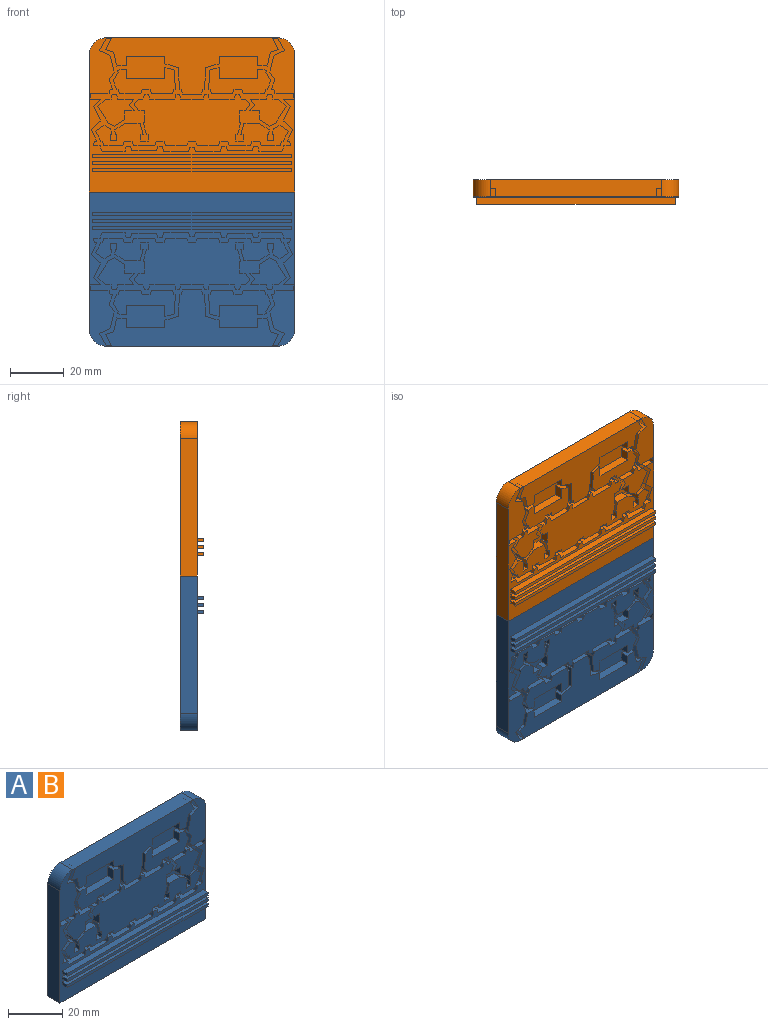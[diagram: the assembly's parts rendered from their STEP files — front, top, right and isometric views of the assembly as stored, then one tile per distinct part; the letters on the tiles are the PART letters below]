
ASSEMBLY  parts=2 mates=1
PART A: 265 faces, bbox 76.2x8.9x57.2 mm
  f0: plane 50.8x6.35mm, normal (1,0,0), area 322.6mm2, adj f2,f5,f262,f263
  f1: plane 50.8x6.35mm, normal (-1,0,0), area 322.6mm2, adj f2,f5,f262,f264
  f2: plane 76.2x57.15mm, normal (0,-1,0), area 1893.1mm2, adj f0,f1,f4,f19,f20,f21,f22,f23
  f3: plane 71.23x19.09mm, normal (0,-1,0), area 830.7mm2, adj f54,f55,f56,f57,f58,f59,f60,f61
  f4: plane 63.5x6.35mm, normal (0,0,1), area 403.2mm2, adj f2,f5,f263,f264
  f5: plane 76.2x57.15mm, normal (0,1,0), area 4337.5mm2, adj f0,f1,f4,f262,f263,f264
  f6: plane 3.18x2.01mm, normal (0.75,0,0.66), area 8.5mm2, adj f7,f125,f126,f128
  f7: plane 3.5x3.18mm, normal (0,0,-1), area 11.1mm2, adj f6,f8,f126,f128
  f8: plane 3.26x3.18mm, normal (1,0,0), area 10.4mm2, adj f7,f9,f126,f128
  f9: plane 3.89x3.18mm, normal (0.54,0,-0.84), area 14.7mm2, adj f8,f10,f126,f128
  f10: plane 3.18x2.64mm, normal (-0.42,0,-0.91), area 9.2mm2, adj f9,f11,f126,f128
  f11: plane 3.18x0.74mm, normal (-1,0,0), area 2.3mm2, adj f10,f12,f126,f128
  f12: plane 5.23x3.4mm, normal (-0.84,0,-0.54), area 19.8mm2, adj f11,f13,f126,f128
  f13: plane 3.18x2.9mm, normal (-0.73,0,0.68), area 12.6mm2, adj f12,f14,f126,f128
  f14: plane 3.18x2.21mm, normal (0,0,1), area 7mm2, adj f13,f15,f126,f128
  f15: plane 3.18x1.66mm, normal (-0.98,0,0.22), area 5.4mm2, adj f14,f16,f126,f128
  f16: plane 3.18x1.63mm, normal (0,0,1), area 5.2mm2, adj f15,f17,f126,f128
  f17: plane 3.18x1.71mm, normal (0.97,0,0.22), area 5.6mm2, adj f16,f18,f126,f128
  f18: plane 5.87x3.18mm, normal (0,0,1), area 18.6mm2, adj f17,f125,f126,f128
  f19: plane 3.34x3.18mm, normal (1,0,0), area 10.6mm2, adj f2,f20,f123,f126
  f20: plane 3.55x3.18mm, normal (0.09,0,-1), area 11.3mm2, adj f2,f19,f21,f126
  f21: plane 5.11x3.18mm, normal (-0.98,0,-0.22), area 16.6mm2, adj f2,f20,f22,f126
  f22: plane 3.18x3.02mm, normal (-0.32,0,-0.95), area 10.1mm2, adj f2,f21,f23,f126
  f23: plane 4.09x3.18mm, normal (-0.88,0,0.47), area 14.7mm2, adj f2,f22,f24,f126
  f24: plane 3.18x1.89mm, normal (0,0,-1), area 6mm2, adj f2,f23,f25,f126
  f25: plane 4.53x3.18mm, normal (0.87,0,-0.49), area 16.5mm2, adj f2,f24,f26,f126
  f26: plane 3.92x3.18mm, normal (0.38,0,0.92), area 13.5mm2, adj f2,f25,f27,f126
  f27: plane 6.3x3.18mm, normal (0.97,0,0.24), area 20.6mm2, adj f2,f26,f28,f126
  f28: plane 3.18x2.82mm, normal (0.84,0,-0.54), area 10.6mm2, adj f2,f27,f29,f126
  f29: plane 3.56x3.18mm, normal (0.95,0,0.31), area 11.9mm2, adj f2,f28,f30,f126
  f30: plane 3.18x0.85mm, normal (0,0,-1), area 2.7mm2, adj f2,f29,f31,f126
  f31: plane 3.18x1.61mm, normal (0.97,0,-0.24), area 5.3mm2, adj f2,f30,f32,f126
  f32: plane 6.85x3.18mm, normal (0,0,-1), area 21.7mm2, adj f2,f31,f33,f126
  f33: plane 3.18x2.02mm, normal (1,0,0), area 6.4mm2, adj f2,f32,f34,f126
  f34: plane 3.8x3.18mm, normal (0,0,1), area 12mm2, adj f2,f33,f35,f126
  f35: plane 3.18x2.65mm, normal (0.7,0,-0.71), area 11.8mm2, adj f2,f34,f36,f126
  f36: plane 5.53x3.18mm, normal (0.9,0,0.43), area 19.5mm2, adj f2,f35,f37,f126
  f37: plane 3.53x3.18mm, normal (0.66,0,-0.75), area 14.9mm2, adj f2,f36,f38,f126
  f38: plane 4.4x3.18mm, normal (0.92,0,0.4), area 15.3mm2, adj f2,f37,f39,f126
  f39: plane 3.18x0.74mm, normal (0,0,-1), area 2.4mm2, adj f2,f38,f40,f126
  f40: plane 3.18x1.73mm, normal (0.97,0,-0.23), area 5.6mm2, adj f2,f39,f41,f126
  f41: plane 3.18x2.55mm, normal (0,0,1), area 8.1mm2, adj f2,f40,f42,f126
  f42: plane 3.18x1.98mm, normal (0.94,0,0.34), area 6.7mm2, adj f2,f41,f43,f126
  f43: plane 8.49x3.18mm, normal (0,0,1), area 27mm2, adj f2,f42,f44,f126
  f44: plane 3.18x1.83mm, normal (-0.98,0,0.22), area 5.9mm2, adj f2,f43,f45,f126
  f45: plane 3.18x1.59mm, normal (0,0,1), area 5mm2, adj f2,f44,f46,f126
  f46: plane 3.18x1.72mm, normal (0.96,0,0.28), area 5.7mm2, adj f2,f45,f47,f126
  f47: plane 9.21x3.18mm, normal (0,0,1), area 29.3mm2, adj f2,f46,f48,f126
  f48: plane 3.18x1.77mm, normal (-0.97,0,0.25), area 5.8mm2, adj f2,f47,f49,f126
  f49: plane 3.18x1.67mm, normal (0,0,1), area 5.3mm2, adj f2,f48,f50,f126
  f50: plane 3.18x1.9mm, normal (0.96,0,0.26), area 6.3mm2, adj f2,f49,f51,f126
  f51: plane 9.18x3.18mm, normal (0,0,1), area 29.1mm2, adj f2,f50,f52,f126
  f52: plane 3.18x1.58mm, normal (-0.96,0,0.29), area 5.2mm2, adj f2,f51,f53,f126
  f53: plane 3.18x1.59mm, normal (0,0,1), area 5.1mm2, adj f2,f52,f126,f193
  f54: plane 3.18x2.87mm, normal (0,0,-1), area 9.1mm2, adj f3,f55,f126,f192
  f55: plane 3.18x1.43mm, normal (0.92,0,-0.39), area 4.9mm2, adj f3,f54,f56,f126
  f56: plane 7.75x3.18mm, normal (0,0,-1), area 24.6mm2, adj f3,f55,f57,f126
  f57: plane 3.18x1.57mm, normal (-0.94,0,-0.35), area 5.3mm2, adj f3,f56,f58,f126
  f58: plane 3.18x2.88mm, normal (0,0,-1), area 9.1mm2, adj f3,f57,f59,f126
  f59: plane 3.18x1.66mm, normal (0.95,0,-0.32), area 5.6mm2, adj f3,f58,f60,f126
  f60: plane 7.75x3.18mm, normal (0,0,-1), area 24.6mm2, adj f3,f59,f61,f126
  f61: plane 3.18x1.63mm, normal (-0.93,0,-0.37), area 5.6mm2, adj f3,f60,f62,f126
  f62: plane 3.18x2.89mm, normal (0,0,-1), area 9.2mm2, adj f3,f61,f63,f126
  f63: plane 3.18x1.59mm, normal (0.94,0,-0.35), area 5.4mm2, adj f3,f62,f64,f126
  f64: plane 7.01x3.18mm, normal (0,0,-1), area 22.3mm2, adj f3,f63,f65,f126
  f65: plane 3.18x1.66mm, normal (-0.97,0,-0.26), area 5.5mm2, adj f3,f64,f66,f126
  f66: plane 3.18x0.65mm, normal (0,0,-1), area 2.1mm2, adj f3,f65,f67,f126
  f67: plane 3.61x3.18mm, normal (-0.89,0,-0.45), area 12.8mm2, adj f3,f66,f68,f126
  f68: plane 3.18x3mm, normal (-0.61,0,0.79), area 12mm2, adj f3,f67,f69,f126
  f69: plane 3.18x2.52mm, normal (0.47,0,0.88), area 9mm2, adj f3,f68,f70,f126
  f70: plane 3.18x2.03mm, normal (0.99,0,0.1), area 6.5mm2, adj f3,f69,f71,f126
  f71: plane 3.18x0.38mm, normal (0,0,-1), area 1.2mm2, adj f3,f70,f72,f126
  f72: plane 3.18x2.39mm, normal (1,0,0), area 7.6mm2, adj f3,f71,f73,f126
  f73: plane 3.18x2.43mm, normal (0,0,1), area 7.7mm2, adj f3,f72,f74,f126
  f74: plane 3.18x2.39mm, normal (-1,0,0), area 7.6mm2, adj f3,f73,f75,f126
  f75: plane 3.18x0.57mm, normal (0,0,-1), area 1.8mm2, adj f3,f74,f76,f126
  f76: plane 3.18x1.63mm, normal (-0.99,0,-0.13), area 5.2mm2, adj f3,f75,f77,f126
  f77: plane 3.94x3.18mm, normal (-0.54,0,0.84), area 14.9mm2, adj f3,f76,f78,f126
  f78: plane 5.46x3.18mm, normal (0,0,1), area 17.3mm2, adj f3,f77,f79,f126
  f79: plane 4.19x3.18mm, normal (0.97,0,0.26), area 13.8mm2, adj f3,f78,f80,f126
  f80: plane 3.18x0.82mm, normal (0,0,-1), area 2.6mm2, adj f3,f79,f81,f126
  f81: plane 3.18x2.52mm, normal (1,0,0), area 8mm2, adj f3,f80,f82,f126
  f82: plane 3.18x2.61mm, normal (0,0,1), area 8.3mm2, adj f3,f81,f83,f126
  f83: plane 3.18x2.52mm, normal (-1,0,0), area 8mm2, adj f3,f82,f84,f126
  f84: plane 3.18x0.62mm, normal (0,0,-1), area 2mm2, adj f3,f83,f85,f126
  f85: plane 4.33x3.18mm, normal (-0.97,0,-0.26), area 14.2mm2, adj f3,f84,f86,f126
  f86: plane 3.18x0.53mm, normal (0,0,1), area 1.7mm2, adj f3,f85,f87,f126
  f87: plane 4.44x3.18mm, normal (-1,0,0), area 14.1mm2, adj f3,f86,f88,f126
  f88: plane 3.18x2.2mm, normal (0,0,-1), area 7mm2, adj f3,f87,f89,f126
  f89: plane 3.18x2.35mm, normal (-0.81,0,-0.59), area 9.2mm2, adj f3,f88,f90,f126
  f90: plane 3.18x1.95mm, normal (-0.79,0,0.62), area 7.9mm2, adj f3,f89,f91,f126
  f91: plane 3.18x1.76mm, normal (0,0,1), area 5.6mm2, adj f3,f90,f92,f126
  f92: plane 3.18x1.74mm, normal (-0.95,0,0.31), area 5.8mm2, adj f3,f91,f93,f126
  f93: plane 3.18x1.41mm, normal (0,0,1), area 4.5mm2, adj f3,f92,f94,f126
  f94: plane 3.18x1.78mm, normal (0.95,0,0.3), area 5.9mm2, adj f3,f93,f95,f126
  f95: plane 9.25x3.18mm, normal (0,0,1), area 29.4mm2, adj f3,f94,f96,f126
  f96: plane 3.18x1.79mm, normal (-0.97,0,0.23), area 5.8mm2, adj f3,f95,f97,f126
  f97: plane 3.18x1.4mm, normal (0,0,1), area 4.4mm2, adj f3,f96,f98,f126
  f98: plane 3.18x1.79mm, normal (0.97,0,0.24), area 5.8mm2, adj f3,f97,f99,f126
  f99: plane 8.24x3.18mm, normal (0,0,1), area 26.2mm2, adj f3,f98,f126,f149
  f100: plane 7.08x3.18mm, normal (0,0,-1), area 22.5mm2, adj f2,f101,f126,f148
  f101: plane 3.18x1.81mm, normal (-0.97,0,-0.26), area 5.9mm2, adj f2,f100,f102,f126
  f102: plane 3.18x0.62mm, normal (0,0,-1), area 2mm2, adj f2,f101,f103,f126
  f103: plane 8.01x3.18mm, normal (-1,0,-0.05), area 25.5mm2, adj f2,f102,f104,f126
  f104: plane 4.97x3.18mm, normal (-0.28,0,-0.96), area 16.4mm2, adj f2,f103,f105,f126
  f105: plane 3.18x2.85mm, normal (-1,0,0), area 9mm2, adj f2,f104,f123,f126
  f106: plane 3.18x3.13mm, normal (-0.12,0,0.99), area 10mm2, adj f107,f124,f126,f127
  f107: plane 3.51x3.18mm, normal (1,0,0), area 11.1mm2, adj f106,f108,f126,f127
  f108: plane 14.32x3.18mm, normal (0,0,1), area 45.5mm2, adj f107,f109,f126,f127
  f109: plane 4.18x3.18mm, normal (-1,0,0), area 13.3mm2, adj f108,f110,f126,f127
  f110: plane 3.51x3.18mm, normal (0.29,0,0.96), area 11.6mm2, adj f109,f111,f126,f127
  f111: plane 7.06x3.18mm, normal (1,0,0.05), area 22.4mm2, adj f110,f112,f126,f127
  f112: plane 3.18x0.6mm, normal (0,0,-1), area 1.9mm2, adj f111,f113,f126,f127
  f113: plane 3.18x1.65mm, normal (0.97,0,-0.22), area 5.4mm2, adj f112,f114,f126,f127
  f114: plane 7.82x3.18mm, normal (0,0,-1), area 24.8mm2, adj f113,f115,f126,f127
  f115: plane 3.18x1.65mm, normal (-0.95,0,-0.32), area 5.5mm2, adj f114,f116,f126,f127
  f116: plane 3.18x2.96mm, normal (0,0,-1), area 9.4mm2, adj f115,f117,f126,f127
  f117: plane 3.18x1.69mm, normal (0.96,0,-0.29), area 5.6mm2, adj f116,f118,f126,f127
  f118: plane 7.77x3.18mm, normal (0,0,-1), area 24.7mm2, adj f117,f119,f126,f127
  f119: plane 3.18x1.69mm, normal (-0.94,0,-0.34), area 5.7mm2, adj f118,f120,f126,f127
  f120: plane 3.18x0.57mm, normal (0,0,-1), area 1.8mm2, adj f119,f121,f126,f127
  f121: plane 3.18x3.13mm, normal (-0.94,0,-0.35), area 10.6mm2, adj f120,f122,f126,f127
  f122: plane 3.18x3.08mm, normal (-0.87,0,0.49), area 11.2mm2, adj f121,f124,f126,f127
  f123: plane 14.32x3.18mm, normal (0,0,-1), area 45.5mm2, adj f2,f19,f105,f126
  f124: plane 3.18x0.85mm, normal (-0.99,0,-0.12), area 2.7mm2, adj f106,f122,f126,f127
  f125: plane 3.18x2.24mm, normal (0.82,0,-0.57), area 8.6mm2, adj f6,f18,f126,f128
  f126: plane 75.21x41.83mm, normal (0,-1,0), area 876.6mm2, adj f6,f7,f8,f9,f10,f11,f12,f13
  f127: plane 22.95x9.8mm, normal (0,-1,0), area 140.1mm2, adj f106,f107,f108,f109,f110,f111,f112,f113
  f128: plane 13.42x11.75mm, normal (0,-1,0), area 88.1mm2, adj f6,f7,f8,f9,f10,f11,f12,f13
  f129: plane 3.18x2.01mm, normal (-0.75,0,0.66), area 8.5mm2, adj f126,f130,f244,f246
  f130: plane 3.18x2.24mm, normal (-0.82,0,-0.57), area 8.6mm2, adj f126,f129,f131,f246
  f131: plane 5.87x3.18mm, normal (0,0,1), area 18.6mm2, adj f126,f130,f132,f246
  f132: plane 3.18x1.71mm, normal (-0.97,0,0.22), area 5.6mm2, adj f126,f131,f133,f246
  f133: plane 3.18x1.63mm, normal (0,0,1), area 5.2mm2, adj f126,f132,f134,f246
  f134: plane 3.18x1.66mm, normal (0.98,0,0.22), area 5.4mm2, adj f126,f133,f135,f246
  f135: plane 3.18x2.21mm, normal (0,0,1), area 7mm2, adj f126,f134,f136,f246
  f136: plane 3.18x2.9mm, normal (0.73,0,0.68), area 12.6mm2, adj f126,f135,f137,f246
  f137: plane 5.23x3.4mm, normal (0.84,0,-0.54), area 19.8mm2, adj f126,f136,f138,f246
  f138: plane 3.18x0.74mm, normal (1,0,0), area 2.3mm2, adj f126,f137,f139,f246
  f139: plane 3.18x2.64mm, normal (0.42,0,-0.91), area 9.2mm2, adj f126,f138,f140,f246
  f140: plane 3.89x3.18mm, normal (-0.54,0,-0.84), area 14.7mm2, adj f126,f139,f141,f246
  f141: plane 3.26x3.18mm, normal (-1,0,0), area 10.4mm2, adj f126,f140,f244,f246
  f142: plane 3.34x3.18mm, normal (-1,0,0), area 10.6mm2, adj f2,f126,f143,f242
  f143: plane 14.32x3.18mm, normal (0,0,-1), area 45.5mm2, adj f2,f126,f142,f144
  f144: plane 3.18x2.85mm, normal (1,0,0), area 9mm2, adj f2,f126,f143,f145
  f145: plane 4.97x3.18mm, normal (0.28,0,-0.96), area 16.4mm2, adj f2,f126,f144,f146
  f146: plane 8.01x3.18mm, normal (1,0,-0.05), area 25.5mm2, adj f2,f126,f145,f147
  f147: plane 3.18x0.62mm, normal (0,0,-1), area 2mm2, adj f2,f126,f146,f148
  f148: plane 3.18x1.81mm, normal (0.97,0,-0.26), area 5.9mm2, adj f2,f100,f126,f147
  f149: plane 3.18x1.79mm, normal (-0.97,0,0.24), area 5.8mm2, adj f3,f99,f126,f150
  f150: plane 3.18x1.4mm, normal (0,0,1), area 4.4mm2, adj f3,f126,f149,f151
  f151: plane 3.18x1.79mm, normal (0.97,0,0.23), area 5.8mm2, adj f3,f126,f150,f152
  f152: plane 9.25x3.18mm, normal (0,0,1), area 29.4mm2, adj f3,f126,f151,f153
  f153: plane 3.18x1.78mm, normal (-0.95,0,0.3), area 5.9mm2, adj f3,f126,f152,f154
  f154: plane 3.18x1.41mm, normal (0,0,1), area 4.5mm2, adj f3,f126,f153,f155
  f155: plane 3.18x1.74mm, normal (0.95,0,0.31), area 5.8mm2, adj f3,f126,f154,f156
  f156: plane 3.18x1.76mm, normal (0,0,1), area 5.6mm2, adj f3,f126,f155,f157
  f157: plane 3.18x1.95mm, normal (0.79,0,0.62), area 7.9mm2, adj f3,f126,f156,f158
  f158: plane 3.18x2.35mm, normal (0.81,0,-0.59), area 9.2mm2, adj f3,f126,f157,f159
  f159: plane 3.18x2.2mm, normal (0,0,-1), area 7mm2, adj f3,f126,f158,f160
  f160: plane 4.44x3.18mm, normal (1,0,0), area 14.1mm2, adj f3,f126,f159,f161
  f161: plane 3.18x0.53mm, normal (0,0,1), area 1.7mm2, adj f3,f126,f160,f162
  f162: plane 4.33x3.18mm, normal (0.97,0,-0.26), area 14.2mm2, adj f3,f126,f161,f163
  f163: plane 3.18x0.62mm, normal (0,0,-1), area 2mm2, adj f3,f126,f162,f164
  f164: plane 3.18x2.52mm, normal (1,0,0), area 8mm2, adj f3,f126,f163,f165
  f165: plane 3.18x2.61mm, normal (0,0,1), area 8.3mm2, adj f3,f126,f164,f166
  f166: plane 3.18x2.52mm, normal (-1,0,0), area 8mm2, adj f3,f126,f165,f167
  f167: plane 3.18x0.82mm, normal (0,0,-1), area 2.6mm2, adj f3,f126,f166,f168
  f168: plane 4.19x3.18mm, normal (-0.97,0,0.26), area 13.8mm2, adj f3,f126,f167,f169
  f169: plane 5.46x3.18mm, normal (0,0,1), area 17.3mm2, adj f3,f126,f168,f170
  f170: plane 3.94x3.18mm, normal (0.54,0,0.84), area 14.9mm2, adj f3,f126,f169,f171
  f171: plane 3.18x1.63mm, normal (0.99,0,-0.13), area 5.2mm2, adj f3,f126,f170,f172
  f172: plane 3.18x0.57mm, normal (0,0,-1), area 1.8mm2, adj f3,f126,f171,f173
  f173: plane 3.18x2.39mm, normal (1,0,0), area 7.6mm2, adj f3,f126,f172,f174
  f174: plane 3.18x2.43mm, normal (0,0,1), area 7.7mm2, adj f3,f126,f173,f175
  f175: plane 3.18x2.39mm, normal (-1,0,0), area 7.6mm2, adj f3,f126,f174,f176
  f176: plane 3.18x0.38mm, normal (0,0,-1), area 1.2mm2, adj f3,f126,f175,f177
  f177: plane 3.18x2.03mm, normal (-0.99,0,0.1), area 6.5mm2, adj f3,f126,f176,f178
  f178: plane 3.18x2.52mm, normal (-0.47,0,0.88), area 9mm2, adj f3,f126,f177,f179
  f179: plane 3.18x3mm, normal (0.61,0,0.79), area 12mm2, adj f3,f126,f178,f180
  f180: plane 3.61x3.18mm, normal (0.89,0,-0.45), area 12.8mm2, adj f3,f126,f179,f181
  f181: plane 3.18x0.65mm, normal (0,0,-1), area 2.1mm2, adj f3,f126,f180,f182
  f182: plane 3.18x1.66mm, normal (0.97,0,-0.26), area 5.5mm2, adj f3,f126,f181,f183
  f183: plane 7.01x3.18mm, normal (0,0,-1), area 22.3mm2, adj f3,f126,f182,f184
  f184: plane 3.18x1.59mm, normal (-0.94,0,-0.35), area 5.4mm2, adj f3,f126,f183,f185
  f185: plane 3.18x2.89mm, normal (0,0,-1), area 9.2mm2, adj f3,f126,f184,f186
  f186: plane 3.18x1.63mm, normal (0.93,0,-0.37), area 5.6mm2, adj f3,f126,f185,f187
  f187: plane 7.75x3.18mm, normal (0,0,-1), area 24.6mm2, adj f3,f126,f186,f188
  f188: plane 3.18x1.66mm, normal (-0.95,0,-0.32), area 5.6mm2, adj f3,f126,f187,f189
  f189: plane 3.18x2.88mm, normal (0,0,-1), area 9.1mm2, adj f3,f126,f188,f190
  f190: plane 3.18x1.57mm, normal (0.94,0,-0.35), area 5.3mm2, adj f3,f126,f189,f191
  f191: plane 7.75x3.18mm, normal (0,0,-1), area 24.6mm2, adj f3,f126,f190,f192
  f192: plane 3.18x1.43mm, normal (-0.92,0,-0.39), area 4.9mm2, adj f3,f54,f126,f191
  f193: plane 3.18x1.58mm, normal (0.96,0,0.29), area 5.2mm2, adj f2,f53,f126,f194
  f194: plane 9.18x3.18mm, normal (0,0,1), area 29.1mm2, adj f2,f126,f193,f195
  f195: plane 3.18x1.9mm, normal (-0.96,0,0.26), area 6.3mm2, adj f2,f126,f194,f196
  f196: plane 3.18x1.67mm, normal (0,0,1), area 5.3mm2, adj f2,f126,f195,f197
  f197: plane 3.18x1.77mm, normal (0.97,0,0.25), area 5.8mm2, adj f2,f126,f196,f198
  f198: plane 9.21x3.18mm, normal (0,0,1), area 29.3mm2, adj f2,f126,f197,f199
  f199: plane 3.18x1.72mm, normal (-0.96,0,0.28), area 5.7mm2, adj f2,f126,f198,f200
  f200: plane 3.18x1.59mm, normal (0,0,1), area 5mm2, adj f2,f126,f199,f201
  f201: plane 3.18x1.83mm, normal (0.98,0,0.22), area 5.9mm2, adj f2,f126,f200,f202
  f202: plane 8.49x3.18mm, normal (0,0,1), area 27mm2, adj f2,f126,f201,f203
  f203: plane 3.18x1.98mm, normal (-0.94,0,0.34), area 6.7mm2, adj f2,f126,f202,f204
  f204: plane 3.18x2.55mm, normal (0,0,1), area 8.1mm2, adj f2,f126,f203,f205
  f205: plane 3.18x1.73mm, normal (-0.97,0,-0.23), area 5.6mm2, adj f2,f126,f204,f206
  f206: plane 3.18x0.74mm, normal (0,0,-1), area 2.4mm2, adj f2,f126,f205,f207
  f207: plane 4.4x3.18mm, normal (-0.92,0,0.4), area 15.3mm2, adj f2,f126,f206,f208
  f208: plane 3.53x3.18mm, normal (-0.66,0,-0.75), area 14.9mm2, adj f2,f126,f207,f209
  f209: plane 5.53x3.18mm, normal (-0.9,0,0.43), area 19.5mm2, adj f2,f126,f208,f210
  f210: plane 3.18x2.65mm, normal (-0.7,0,-0.71), area 11.8mm2, adj f2,f126,f209,f211
  f211: plane 3.8x3.18mm, normal (0,0,1), area 12mm2, adj f2,f126,f210,f212
  f212: plane 3.18x2.02mm, normal (-1,0,0), area 6.4mm2, adj f2,f126,f211,f213
  f213: plane 6.85x3.18mm, normal (0,0,-1), area 21.7mm2, adj f2,f126,f212,f214
  f214: plane 3.18x1.61mm, normal (-0.97,0,-0.24), area 5.3mm2, adj f2,f126,f213,f215
  f215: plane 3.18x0.85mm, normal (0,0,-1), area 2.7mm2, adj f2,f126,f214,f216
  f216: plane 3.56x3.18mm, normal (-0.95,0,0.31), area 11.9mm2, adj f2,f126,f215,f217
  f217: plane 3.18x2.82mm, normal (-0.84,0,-0.54), area 10.6mm2, adj f2,f126,f216,f218
  f218: plane 6.3x3.18mm, normal (-0.97,0,0.24), area 20.6mm2, adj f2,f126,f217,f219
  f219: plane 3.92x3.18mm, normal (-0.38,0,0.92), area 13.5mm2, adj f2,f126,f218,f220
  f220: plane 4.53x3.18mm, normal (-0.87,0,-0.49), area 16.5mm2, adj f2,f126,f219,f221
  f221: plane 3.18x1.89mm, normal (0,0,-1), area 6mm2, adj f2,f126,f220,f222
  f222: plane 4.09x3.18mm, normal (0.88,0,0.47), area 14.7mm2, adj f2,f126,f221,f223
  f223: plane 3.18x3.02mm, normal (0.32,0,-0.95), area 10.1mm2, adj f2,f126,f222,f224
  f224: plane 5.11x3.18mm, normal (0.98,0,-0.22), area 16.6mm2, adj f2,f126,f223,f242
  f225: plane 3.18x3.13mm, normal (0.12,0,0.99), area 10mm2, adj f126,f226,f243,f245
  f226: plane 3.18x0.85mm, normal (0.99,0,-0.12), area 2.7mm2, adj f126,f225,f227,f245
  f227: plane 3.18x3.08mm, normal (0.87,0,0.49), area 11.2mm2, adj f126,f226,f228,f245
  f228: plane 3.18x3.13mm, normal (0.94,0,-0.35), area 10.6mm2, adj f126,f227,f229,f245
  f229: plane 3.18x0.57mm, normal (0,0,-1), area 1.8mm2, adj f126,f228,f230,f245
  f230: plane 3.18x1.69mm, normal (0.94,0,-0.34), area 5.7mm2, adj f126,f229,f231,f245
  f231: plane 7.77x3.18mm, normal (0,0,-1), area 24.7mm2, adj f126,f230,f232,f245
  f232: plane 3.18x1.69mm, normal (-0.96,0,-0.29), area 5.6mm2, adj f126,f231,f233,f245
  f233: plane 3.18x2.96mm, normal (0,0,-1), area 9.4mm2, adj f126,f232,f234,f245
  f234: plane 3.18x1.65mm, normal (0.95,0,-0.32), area 5.5mm2, adj f126,f233,f235,f245
  f235: plane 7.82x3.18mm, normal (0,0,-1), area 24.8mm2, adj f126,f234,f236,f245
  f236: plane 3.18x1.65mm, normal (-0.97,0,-0.22), area 5.4mm2, adj f126,f235,f237,f245
  f237: plane 3.18x0.6mm, normal (0,0,-1), area 1.9mm2, adj f126,f236,f238,f245
  f238: plane 7.06x3.18mm, normal (-1,0,0.05), area 22.4mm2, adj f126,f237,f239,f245
  f239: plane 3.51x3.18mm, normal (-0.29,0,0.96), area 11.6mm2, adj f126,f238,f240,f245
  f240: plane 4.18x3.18mm, normal (1,0,0), area 13.3mm2, adj f126,f239,f241,f245
  f241: plane 14.32x3.18mm, normal (0,0,1), area 45.5mm2, adj f126,f240,f243,f245
  f242: plane 3.55x3.18mm, normal (-0.09,0,-1), area 11.3mm2, adj f2,f126,f142,f224
  f243: plane 3.51x3.18mm, normal (-1,0,0), area 11.1mm2, adj f126,f225,f241,f245
  f244: plane 3.5x3.18mm, normal (0,0,-1), area 11.1mm2, adj f126,f129,f141,f246
  f245: plane 22.95x9.8mm, normal (0,-1,0), area 140.1mm2, adj f225,f226,f227,f228,f229,f230,f231,f232
  f246: plane 13.42x11.75mm, normal (0,-1,0), area 88.1mm2, adj f129,f130,f131,f132,f133,f134,f135,f136
  f247: plane 2.54x1.27mm, normal (-1,0,0), area 3.2mm2, adj f2,f248,f250,f251
  f248: plane 73.66x2.54mm, normal (0,0,-1), area 187.1mm2, adj f2,f247,f249,f251
  f249: plane 2.54x1.27mm, normal (1,0,0), area 3.2mm2, adj f2,f248,f250,f251
  f250: plane 73.66x2.54mm, normal (0,0,1), area 187.1mm2, adj f2,f247,f249,f251
  f251: plane 73.66x1.27mm, normal (0,-1,0), area 93.5mm2, adj f247,f248,f249,f250
  f252: plane 73.66x2.54mm, normal (0,0,-1), area 187.1mm2, adj f2,f253,f255,f256
  f253: plane 2.54x1.27mm, normal (1,0,0), area 3.2mm2, adj f2,f252,f254,f256
  f254: plane 73.66x2.54mm, normal (0,0,1), area 187.1mm2, adj f2,f253,f255,f256
  f255: plane 2.54x1.27mm, normal (-1,0,0), area 3.2mm2, adj f2,f252,f254,f256
  f256: plane 73.66x1.27mm, normal (0,-1,0), area 93.5mm2, adj f252,f253,f254,f255
  f257: plane 2.54x1.27mm, normal (1,0,0), area 3.2mm2, adj f2,f258,f260,f261
  f258: plane 73.66x2.54mm, normal (0,0,1), area 187.1mm2, adj f2,f257,f259,f261
  f259: plane 2.54x1.27mm, normal (-1,0,0), area 3.2mm2, adj f2,f258,f260,f261
  f260: plane 73.66x2.54mm, normal (0,0,-1), area 187.1mm2, adj f2,f257,f259,f261
  f261: plane 73.66x1.27mm, normal (0,-1,0), area 93.5mm2, adj f257,f258,f259,f260
  f262: plane 76.2x6.35mm, normal (0,0,-1), area 483.9mm2, adj f0,f1,f2,f5
  f263: cylinder r=6.35mm len=6.35mm, axis (0,1,0), area 63.3mm2, adj f0,f2,f4,f5
  f264: cylinder r=6.35mm len=6.35mm, axis (0,-1,0), area 63.3mm2, adj f1,f2,f4,f5
PART B: same geometry as A
PLACE A rot(axis=(0,1,0),180deg) t=(10.55,34.99,22.39)mm
PLACE B t=(10.55,34.99,-15.71)mm
MATE parallel A.f262 <-> B.f262  axis (0,0,1) through (10.55,31.81,3.34)mm
